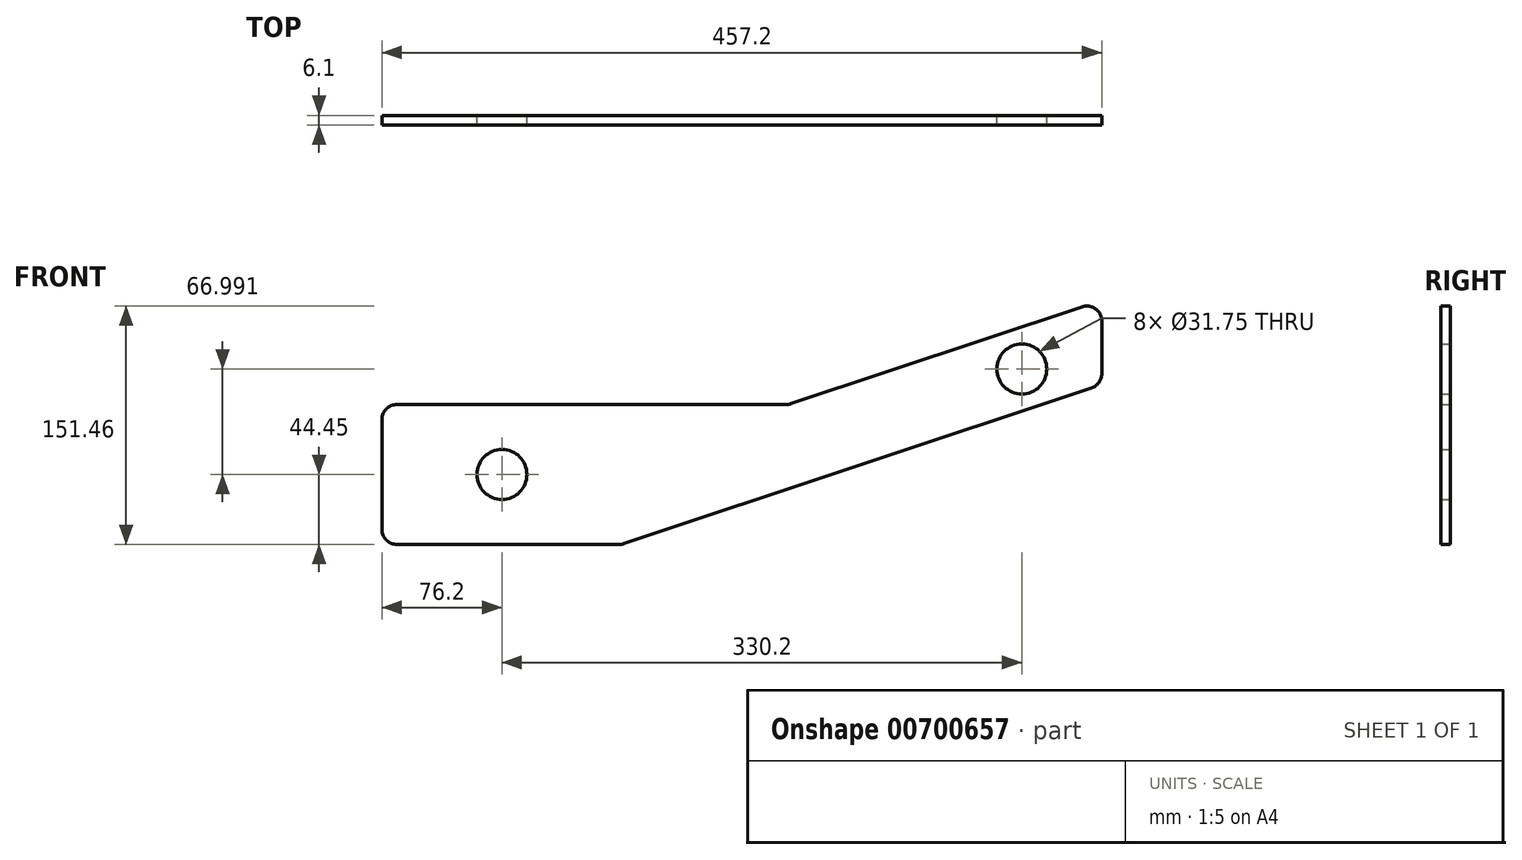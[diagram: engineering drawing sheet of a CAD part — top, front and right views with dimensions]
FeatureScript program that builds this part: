
annotation { "Feature Type Name" : "Feature", "Feature Type Description" : "" }
export const myFeature = defineFeature(function(context is Context, id is Id, definition is map)
    precondition{}
    {
        {
            var Q0;
            Q0=qCreatedBy(makeId("Front.planeOp"),FACE);
            var sketch = newSketch(context, id + "F0", { "sketchPlane" : qUnion([Q0])});
            skLineSegment(sketch, "E0.bottom", {"start": v(0, 0) * mm, "end": v(152.4, 0) * mm});
            skLineSegment(sketch, "E0.top", {"start": v(0, 88.9) * mm, "end": v(152.4, 88.9) * mm});
            skLineSegment(sketch, "E0.left", {"start": v(0, 0) * mm, "end": v(0, 88.9) * mm});
            skLineSegment(sketch, "E0.right", {"start": v(152.4, 0) * mm, "end": v(152.4, 88.9) * mm, "construction": true});
            skLineSegment(sketch, "E1", {"start": v(152.4, 0) * mm, "end": v(457.2, 101.6) * mm});
            skLineSegment(sketch, "E2", {"start": v(457.2, 101.6) * mm, "end": v(457.2, 155.15) * mm});
            skLineSegment(sketch, "E3", {"start": v(152.4, 0) * mm, "end": v(457.2, 0) * mm, "construction": true});
            skLineSegment(sketch, "E4", {"start": v(457.2, 0) * mm, "end": v(457.2, 101.6) * mm, "construction": true});
            skLineSegment(sketch, "E5", {"start": v(152.4, 53.55) * mm, "end": v(258.46, 88.9) * mm, "construction": true});
            skLineSegment(sketch, "E6", {"start": v(152.4, 88.9) * mm, "end": v(258.46, 88.9) * mm});
            skLineSegment(sketch, "E7", {"start": v(258.46, 88.9) * mm, "end": v(457.2, 155.15) * mm});
            skCircle(sketch, "E8", {"center": v(76.2, 44.45) * mm, "radius": 15.88 * mm});
            skPoint(sketch, "E8.centerSnap0", {"position": v(0, 44.45) * mm});
            skCircle(sketch, "E9", {"center": v(406.4, 111.44) * mm, "radius": 15.88 * mm});
            skLineSegment(sketch, "E10", {"start": v(0, 44.45) * mm, "end": v(76.2, 44.45) * mm, "construction": true});
            skLineSegment(sketch, "E11", {"start": v(406.4, 111.44) * mm, "end": v(457.2, 128.37) * mm, "construction": true});
            skSolve(sketch);
        }
        {
            var Q0;
            Q0 = qSketchRegion(id + "F0", true);
            extrude(context, id + "F1", {"entities" : qUnion([Q0]), "depth" : 6.1 * mm, "offsetDistance" : 25.4 * mm});
        }
        {
            var Q0;
            Q0=makeQuery(id+"F1.opExtrude","SWEPT_EDGE",EDGE,{"disambiguationData":[OSD([sQuery(id+"F0.wireOp",EDGE,"E1"),sQuery(id+"F0.wireOp",EDGE,"E2")])]});
            var Q1;
            Q1=makeQuery(id+"F1.opExtrude","SWEPT_EDGE",EDGE,{"disambiguationData":[OSD([sQuery(id+"F0.wireOp",EDGE,"E2"),sQuery(id+"F0.wireOp",EDGE,"E7")])]});
            var Q2;
            Q2=makeQuery(id+"F1.opExtrude","SWEPT_EDGE",EDGE,{"disambiguationData":[OSD([sQuery(id+"F0.wireOp",EDGE,"E6"),sQuery(id+"F0.wireOp",EDGE,"E7")])]});
            var Q3;
            Q3=makeQuery(id+"F1.opExtrude","SWEPT_EDGE",EDGE,{"disambiguationData":[OSD([sQuery(id+"F0.wireOp",EDGE,"E0.top"),sQuery(id+"F0.wireOp",EDGE,"E0.left")])]});
            var Q4;
            Q4=makeQuery(id+"F1.opExtrude","SWEPT_EDGE",EDGE,{"disambiguationData":[OSD([sQuery(id+"F0.wireOp",EDGE,"E0.bottom"),sQuery(id+"F0.wireOp",EDGE,"E0.left")])]});
            var Q5;
            Q5=makeQuery(id+"F1.opExtrude","SWEPT_EDGE",EDGE,{"disambiguationData":[OSD([sQuery(id+"F0.wireOp",EDGE,"E0.bottom"),sQuery(id+"F0.wireOp",EDGE,"E1")])]});
            fillet(context, id + "F2", {"entities" : qUnion([Q0, Q1, Q2, Q3, Q4, Q5]), "radius" : 9.52 * mm, "tangentPropagation" : true, "allowEdgeOverflow" : false});
        }
    });
